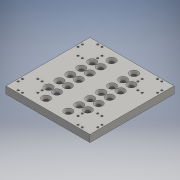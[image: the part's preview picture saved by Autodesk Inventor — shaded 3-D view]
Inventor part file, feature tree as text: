
AUTODESK INVENTOR PART (.ipt)
format: ipt  version: 2016 (Build 200138000, 138)  size: 221,184 bytes
history: native  units: mm
features: sketch x4, hole x3, extrude x1
ambient origin geometry x8: Origin, YZ Plane, XZ Plane, XY Plane, X Axis, Y Axis, Z Axis, Center Point
bodies: Solid1 (feature_tree)
feature tree (8):
  extrude  "Extrusion1"  Depth=75.0mm
  hole  "Hole1"  [1 undecoded]
  hole  "Hole7"  [1 undecoded]
  hole  "Hole8"  [1 undecoded]
  sketch  "Sketch1"  dims[d0=75.0mm d1=75.0mm]
  sketch  "Sketch2"  dims[d2=6.35mm d3=0.0mm d4=21.59mm]
  sketch  "Sketch3"  dims[d5=21.59mm d6=2.032mm]
  sketch  "Sketch4"  dims[d7=12.7mm d8=40.0mm d10=360.0deg d13=40.0mm d15=360.0deg d17=1.694mm d18=4.369mm d19=4.0mm d20=2.0mm d21=90.0deg d22=6.637mm d23=20.594885mm d67=35.0mm d97=18.0mm d112=50.0mm d114=9.75mm d115=10.0mm d117=10.0mm d119=3.797mm d120=7.01mm d121=7.087mm d122=2.0mm d123=14.3117mm d124=10.979mm d125=20.594885mm d126=10.0mm d127=60.0mm d129=9.75mm d130=20.0mm d132=9.75mm d135=3.797mm d136=7.01mm d137=7.087mm d138=2.0mm d139=14.3117mm d140=10.979mm d141=20.594885mm]
note: 3 required parameter values undecoded (feature->parameter linkage not recoverable at this tier; creation-order binding heuristic only, values carry confidence <= 0.55)
